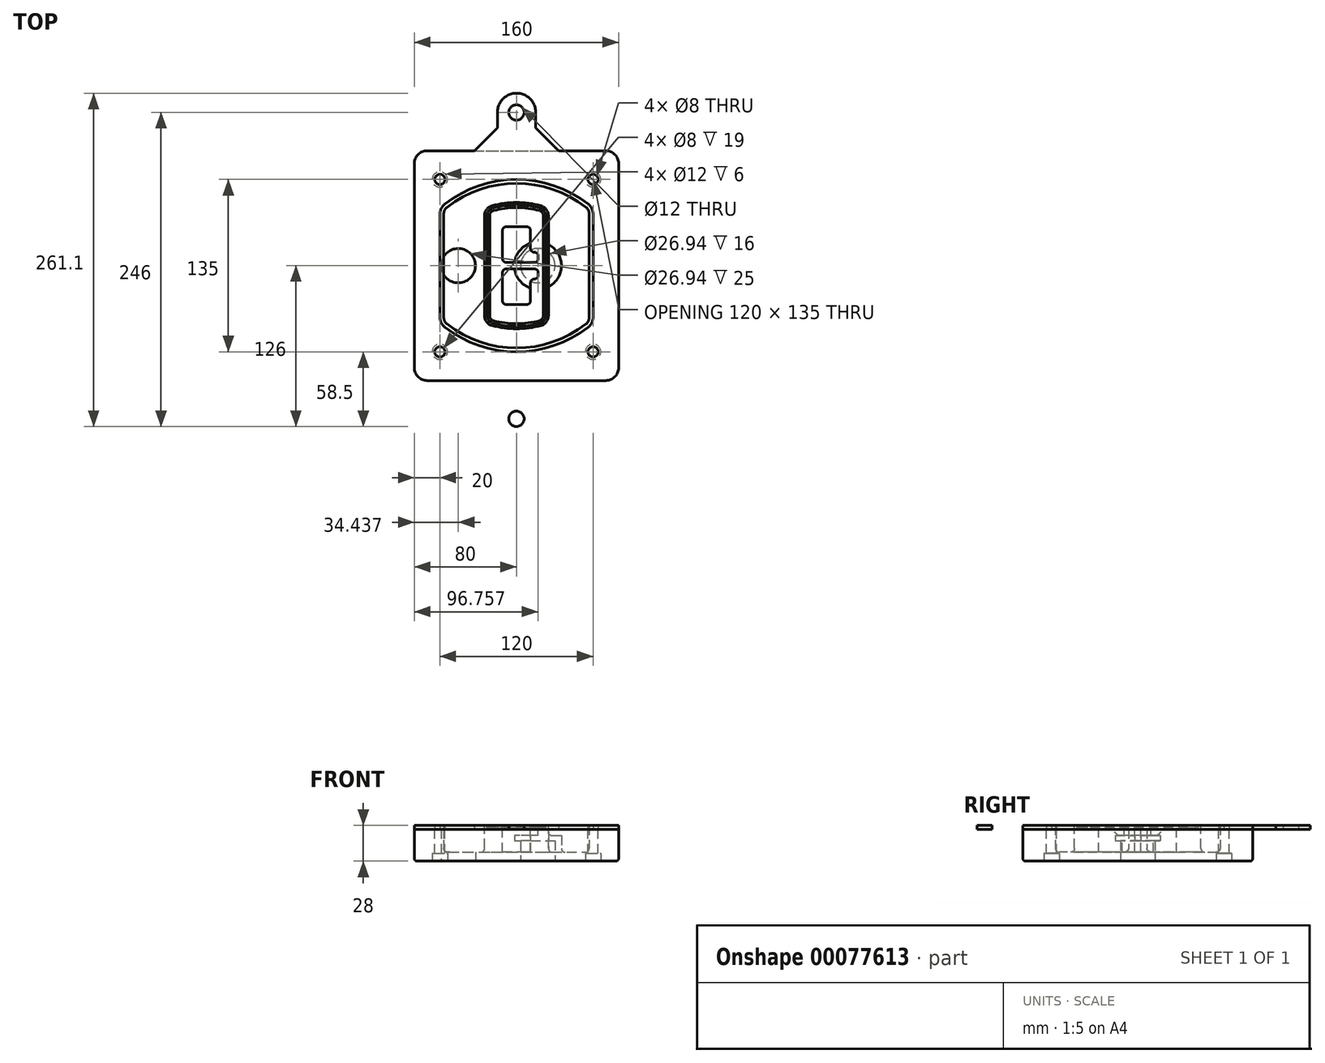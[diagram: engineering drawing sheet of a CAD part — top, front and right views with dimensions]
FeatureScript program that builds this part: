
annotation { "Feature Type Name" : "Feature", "Feature Type Description" : "" }
export const myFeature = defineFeature(function(context is Context, id is Id, definition is map)
    precondition{}
    {
        {
            var Q0;
            Q0=qCreatedBy(makeId("Top.planeOp"),FACE);
            var sketch = newSketch(context, id + "F0", { "sketchPlane" : qUnion([Q0])});
            skPoint(sketch, "E0.rect.middle", {"position": v(0, 0) * mm});
            skLineSegment(sketch, "E1.bottom", {"start": v(-70, -90) * mm, "end": v(70, -90) * mm});
            skLineSegment(sketch, "E1.top", {"start": v(-70, 90) * mm, "end": v(70, 90) * mm});
            skLineSegment(sketch, "E1.left", {"start": v(-80, -80) * mm, "end": v(-80, 80) * mm});
            skLineSegment(sketch, "E1.right", {"start": v(80, -80) * mm, "end": v(80, 80) * mm});
            skLineSegment(sketch, "E2", {"start": v(-80, 90) * mm, "end": v(80, -90) * mm, "construction": true});
            skLineSegment(sketch, "E3", {"start": v(80, 90) * mm, "end": v(-80, -90) * mm, "construction": true});
            skCircle(sketch, "E4", {"center": v(-60, 67.5) * mm, "radius": 4 * mm});
            skCircle(sketch, "E5", {"center": v(60, 67.5) * mm, "radius": 4 * mm});
            skCircle(sketch, "E6", {"center": v(60, -67.5) * mm, "radius": 4 * mm});
            skCircle(sketch, "E7", {"center": v(-60, -67.5) * mm, "radius": 4 * mm});
            skLineSegment(sketch, "E8", {"start": v(-60, 67.5) * mm, "end": v(60, 67.5) * mm, "construction": true});
            skLineSegment(sketch, "E9", {"start": v(60, 67.5) * mm, "end": v(60, -67.5) * mm, "construction": true});
            skLineSegment(sketch, "E10", {"start": v(60, -67.5) * mm, "end": v(-60, -67.5) * mm, "construction": true});
            skLineSegment(sketch, "E11", {"start": v(-60, -67.5) * mm, "end": v(-60, 67.5) * mm, "construction": true});
            skLineSegment(sketch, "E12", {"start": v(-60, 40.3) * mm, "end": v(-60, -40.3) * mm});
            skLineSegment(sketch, "E13", {"start": v(60, 40.3) * mm, "end": v(60, -40.3) * mm});
            skArc(sketch, "E14", {"start": v(56.15, 48.18) * mm, "mid": v(0, 67.5) * mm, "end": v(-56.15, 48.18) * mm});
            skArc(sketch, "E15", {"start": v(-56.15, -48.18) * mm, "mid": v(0, -67.5) * mm, "end": v(56.15, -48.18) * mm});
            skLineSegment(sketch, "E16", {"start": v(-60, 0) * mm, "end": v(60, 0) * mm, "construction": true});
            skPoint(sketch, "E17.visualSharp", {"position": v(-60, -45) * mm});
            skArc(sketch, "E17.filletArc", {"start": v(-60, -40.3) * mm, "mid": v(-58.99, -44.68) * mm, "end": v(-56.15, -48.18) * mm});
            skPoint(sketch, "E18.visualSharp", {"position": v(-60, 45) * mm});
            skArc(sketch, "E18.filletArc", {"start": v(-56.15, 48.18) * mm, "mid": v(-58.99, 44.68) * mm, "end": v(-60, 40.3) * mm});
            skPoint(sketch, "E19.visualSharp", {"position": v(60, 45) * mm});
            skArc(sketch, "E19.filletArc", {"start": v(60, 40.3) * mm, "mid": v(58.99, 44.68) * mm, "end": v(56.15, 48.18) * mm});
            skPoint(sketch, "E20.visualSharp", {"position": v(60, -45) * mm});
            skArc(sketch, "E20.filletArc", {"start": v(56.15, -48.18) * mm, "mid": v(58.99, -44.68) * mm, "end": v(60, -40.3) * mm});
            skPoint(sketch, "E21.visualSharp", {"position": v(-80, 90) * mm});
            skArc(sketch, "E21.filletArc", {"start": v(-70, 90) * mm, "mid": v(-77.07, 87.07) * mm, "end": v(-80, 80) * mm});
            skPoint(sketch, "E22.visualSharp", {"position": v(80, 90) * mm});
            skArc(sketch, "E22.filletArc", {"start": v(80, 80) * mm, "mid": v(77.07, 87.07) * mm, "end": v(70, 90) * mm});
            skPoint(sketch, "E23.visualSharp", {"position": v(80, -90) * mm});
            skArc(sketch, "E23.filletArc", {"start": v(70, -90) * mm, "mid": v(77.07, -87.07) * mm, "end": v(80, -80) * mm});
            skPoint(sketch, "E24.visualSharp", {"position": v(-80, -90) * mm});
            skArc(sketch, "E24.filletArc", {"start": v(-80, -80) * mm, "mid": v(-77.07, -87.07) * mm, "end": v(-70, -90) * mm});
            skArc(sketch, "E25.0", {"start": v(57, 40.3) * mm, "mid": v(56.3, 43.36) * mm, "end": v(54.3, 45.81) * mm});
            skLineSegment(sketch, "E25.1", {"start": v(57, 40.3) * mm, "end": v(57, -40.3) * mm});
            skArc(sketch, "E25.2", {"start": v(54.3, -45.81) * mm, "mid": v(56.3, -43.36) * mm, "end": v(57, -40.3) * mm});
            skArc(sketch, "E25.3", {"start": v(-54.3, -45.81) * mm, "mid": v(0, -64.5) * mm, "end": v(54.3, -45.81) * mm});
            skArc(sketch, "E25.4", {"start": v(-57, -40.3) * mm, "mid": v(-56.3, -43.36) * mm, "end": v(-54.3, -45.81) * mm});
            skArc(sketch, "E25.5", {"start": v(54.3, 45.81) * mm, "mid": v(0, 64.5) * mm, "end": v(-54.3, 45.81) * mm});
            skLineSegment(sketch, "E25.6", {"start": v(-57, 40.3) * mm, "end": v(-57, -40.3) * mm});
            skArc(sketch, "E25.7", {"start": v(-54.3, 45.81) * mm, "mid": v(-56.3, 43.36) * mm, "end": v(-57, 40.3) * mm});
            skArc(sketch, "E26.0", {"start": v(-58.62, 51.33) * mm, "mid": v(-62.58, 46.43) * mm, "end": v(-64, 40.3) * mm});
            skArc(sketch, "E26.1", {"start": v(58.62, 51.33) * mm, "mid": v(0, 71.5) * mm, "end": v(-58.62, 51.33) * mm});
            skArc(sketch, "E26.2", {"start": v(64, 40.3) * mm, "mid": v(62.58, 46.43) * mm, "end": v(58.62, 51.33) * mm});
            skLineSegment(sketch, "E26.3", {"start": v(64, 40.3) * mm, "end": v(64, -40.3) * mm});
            skArc(sketch, "E26.4", {"start": v(58.62, -51.33) * mm, "mid": v(62.58, -46.43) * mm, "end": v(64, -40.3) * mm});
            skLineSegment(sketch, "E26.5", {"start": v(-64, 40.3) * mm, "end": v(-64, -40.3) * mm});
            skArc(sketch, "E26.6", {"start": v(-58.62, -51.33) * mm, "mid": v(0, -71.5) * mm, "end": v(58.62, -51.33) * mm});
            skArc(sketch, "E26.7", {"start": v(-64, -40.3) * mm, "mid": v(-62.58, -46.43) * mm, "end": v(-58.62, -51.33) * mm});
            skSolve(sketch);
        }
        {
            var Q0;
            Q0=makeQuery(id+"F0.imprint","IMPRINT",FACE,{"disambiguationData":[TD([[makeQuery(id+"F0.imprint","IMPRINT",EDGE,{"derivedFrom":sQuery(id+"F0.wireOp",EDGE,"E1.bottom")}),1.0]])]});
            var Q1;
            Q1=makeQuery(id+"F0.imprint","IMPRINT",FACE,{"disambiguationData":[TD([[makeQuery(id+"F0.imprint","IMPRINT",EDGE,{"derivedFrom":sQuery(id+"F0.wireOp",EDGE,"E12")}),1.0]])]});
            var Q2;
            Q2=makeQuery(id+"F0.imprint","IMPRINT",FACE,{"disambiguationData":[TD([[makeQuery(id+"F0.imprint","IMPRINT",EDGE,{"derivedFrom":sQuery(id+"F0.wireOp",EDGE,"E25.0")}),1.0]])]});
            var Q3;
            Q3=makeQuery(id+"F0.imprint","IMPRINT",FACE,{"disambiguationData":[TD([[makeQuery(id+"F0.imprint","IMPRINT",EDGE,{"derivedFrom":sQuery(id+"F0.wireOp",EDGE,"E12")}),-1.0]])]});
            extrude(context, id + "F1", {"entities" : qUnion([Q0, Q1, Q2, Q3]), "oppositeDirection" : true, "depth" : 25 * mm});
        }
        {
            var Q0;
            Q0=makeQuery(id+"F0.imprint","IMPRINT",FACE,{"disambiguationData":[TD([[makeQuery(id+"F0.imprint","IMPRINT",EDGE,{"derivedFrom":sQuery(id+"F0.wireOp",EDGE,"E12")}),1.0]])]});
            extrude(context, id + "F2", {"entities" : qUnion([Q0]), "operationType" : NewBodyOperationType.ADD, "depth" : 3 * mm});
        }
        {
            var Q0;
            Q0=makeQuery(id+"F0.imprint","IMPRINT",FACE,{"disambiguationData":[TD([[makeQuery(id+"F0.imprint","IMPRINT",EDGE,{"derivedFrom":sQuery(id+"F0.wireOp",EDGE,"E25.0")}),1.0]])]});
            extrude(context, id + "F3", {"entities" : qUnion([Q0]), "operationType" : NewBodyOperationType.REMOVE, "oppositeDirection" : true, "depth" : 18 * mm});
        }
        {
            var Q0;
            Q0=makeQuery(id+"F2.opExtrude","CAP_FACE",FACE,{"disambiguationData":[OSD([sQuery(id+"F0.wireOp",EDGE,"E12"),sQuery(id+"F0.wireOp",EDGE,"E13"),sQuery(id+"F0.wireOp",EDGE,"E14"),sQuery(id+"F0.wireOp",EDGE,"E15"),sQuery(id+"F0.wireOp",EDGE,"E17.filletArc"),sQuery(id+"F0.wireOp",EDGE,"E18.filletArc"),sQuery(id+"F0.wireOp",EDGE,"E19.filletArc"),sQuery(id+"F0.wireOp",EDGE,"E20.filletArc"),sQuery(id+"F0.wireOp",EDGE,"E25.0"),sQuery(id+"F0.wireOp",EDGE,"E25.1"),sQuery(id+"F0.wireOp",EDGE,"E25.2"),sQuery(id+"F0.wireOp",EDGE,"E25.3"),sQuery(id+"F0.wireOp",EDGE,"E25.4"),sQuery(id+"F0.wireOp",EDGE,"E25.5"),sQuery(id+"F0.wireOp",EDGE,"E25.6"),sQuery(id+"F0.wireOp",EDGE,"E25.7")])],"isStart":false});
            var sketch = newSketch(context, id + "F4", { "sketchPlane" : qUnion([Q0])});
            skArc(sketch, "E27.0", {"start": v(-19.08, -46.97) * mm, "mid": v(0, -49.5) * mm, "end": v(19.08, -46.97) * mm});
            skArc(sketch, "E28.0", {"start": v(19.08, 46.97) * mm, "mid": v(0, 49.5) * mm, "end": v(-19.08, 46.97) * mm});
            skLineSegment(sketch, "E29", {"start": v(-25, 39.25) * mm, "end": v(-25, -39.25) * mm});
            skLineSegment(sketch, "E30", {"start": v(25, 39.25) * mm, "end": v(25, -39.25) * mm});
            skLineSegment(sketch, "E31", {"start": v(-25, 45.1) * mm, "end": v(25, 45.1) * mm, "construction": true});
            skLineSegment(sketch, "E32", {"start": v(-25, -45.1) * mm, "end": v(25, -45.1) * mm, "construction": true});
            skPoint(sketch, "E33.visualSharp", {"position": v(-25, 45.1) * mm});
            skArc(sketch, "E33.filletArc", {"start": v(-19.08, 46.97) * mm, "mid": v(-23.35, 44.11) * mm, "end": v(-25, 39.25) * mm});
            skPoint(sketch, "E34.visualSharp", {"position": v(25, 45.1) * mm});
            skArc(sketch, "E34.filletArc", {"start": v(25, 39.25) * mm, "mid": v(23.35, 44.11) * mm, "end": v(19.08, 46.97) * mm});
            skPoint(sketch, "E35.visualSharp", {"position": v(25, -45.1) * mm});
            skArc(sketch, "E35.filletArc", {"start": v(19.08, -46.97) * mm, "mid": v(23.35, -44.11) * mm, "end": v(25, -39.25) * mm});
            skPoint(sketch, "E36.visualSharp", {"position": v(-25, -45.1) * mm});
            skArc(sketch, "E36.filletArc", {"start": v(-25, -39.25) * mm, "mid": v(-23.35, -44.11) * mm, "end": v(-19.08, -46.97) * mm});
            skArc(sketch, "E37.0", {"start": v(54.3, 45.81) * mm, "mid": v(0, 64.5) * mm, "end": v(-54.3, 45.81) * mm});
            skArc(sketch, "E37.1", {"start": v(-54.3, 45.81) * mm, "mid": v(-56.3, 43.36) * mm, "end": v(-57, 40.3) * mm});
            skLineSegment(sketch, "E37.2", {"start": v(-57, 40.3) * mm, "end": v(-57, -40.3) * mm});
            skArc(sketch, "E37.3", {"start": v(-57, -40.3) * mm, "mid": v(-56.3, -43.36) * mm, "end": v(-54.3, -45.81) * mm});
            skArc(sketch, "E37.4", {"start": v(-54.3, -45.81) * mm, "mid": v(0, -64.5) * mm, "end": v(54.3, -45.81) * mm});
            skArc(sketch, "E37.5", {"start": v(54.3, -45.81) * mm, "mid": v(56.3, -43.36) * mm, "end": v(57, -40.3) * mm});
            skLineSegment(sketch, "E37.6", {"start": v(57, 40.3) * mm, "end": v(57, -40.3) * mm});
            skArc(sketch, "E37.7", {"start": v(57, 40.3) * mm, "mid": v(56.3, 43.36) * mm, "end": v(54.3, 45.81) * mm});
            skLineSegment(sketch, "E38.0", {"start": v(23, 39.25) * mm, "end": v(23, -39.25) * mm});
            skArc(sketch, "E38.1", {"start": v(18.56, -45.04) * mm, "mid": v(21.76, -42.9) * mm, "end": v(23, -39.25) * mm});
            skArc(sketch, "E38.2", {"start": v(-18.56, -45.04) * mm, "mid": v(0, -47.5) * mm, "end": v(18.56, -45.04) * mm});
            skArc(sketch, "E38.3", {"start": v(-23, -39.25) * mm, "mid": v(-21.76, -42.9) * mm, "end": v(-18.56, -45.04) * mm});
            skLineSegment(sketch, "E38.4", {"start": v(-23, 39.25) * mm, "end": v(-23, -39.25) * mm});
            skArc(sketch, "E38.5", {"start": v(23, 39.25) * mm, "mid": v(21.76, 42.9) * mm, "end": v(18.56, 45.04) * mm});
            skArc(sketch, "E38.6", {"start": v(-18.56, 45.04) * mm, "mid": v(-21.76, 42.9) * mm, "end": v(-23, 39.25) * mm});
            skArc(sketch, "E38.7", {"start": v(18.56, 45.04) * mm, "mid": v(0, 47.5) * mm, "end": v(-18.56, 45.04) * mm});
            skArc(sketch, "E39.0", {"start": v(21, 39.25) * mm, "mid": v(20.18, 41.68) * mm, "end": v(18.04, 43.1) * mm});
            skLineSegment(sketch, "E39.1", {"start": v(21, 39.25) * mm, "end": v(21, -39.25) * mm});
            skArc(sketch, "E39.2", {"start": v(18.04, -43.1) * mm, "mid": v(20.18, -41.68) * mm, "end": v(21, -39.25) * mm});
            skArc(sketch, "E39.3", {"start": v(-18.04, -43.1) * mm, "mid": v(0, -45.5) * mm, "end": v(18.04, -43.1) * mm});
            skArc(sketch, "E39.4", {"start": v(-21, -39.25) * mm, "mid": v(-20.18, -41.68) * mm, "end": v(-18.04, -43.1) * mm});
            skArc(sketch, "E39.5", {"start": v(18.04, 43.1) * mm, "mid": v(0, 45.5) * mm, "end": v(-18.04, 43.1) * mm});
            skLineSegment(sketch, "E39.6", {"start": v(-21, 39.25) * mm, "end": v(-21, -39.25) * mm});
            skArc(sketch, "E39.7", {"start": v(-18.04, 43.1) * mm, "mid": v(-20.18, 41.68) * mm, "end": v(-21, 39.25) * mm});
            skLineSegment(sketch, "E40", {"start": v(-25, 0) * mm, "end": v(25, 0) * mm, "construction": true});
            skLineSegment(sketch, "E41", {"start": v(-11, 5.5) * mm, "end": v(-11, 27.5) * mm});
            skLineSegment(sketch, "E42", {"start": v(-8, 30.5) * mm, "end": v(8, 30.5) * mm});
            skLineSegment(sketch, "E43", {"start": v(11, 27.5) * mm, "end": v(11, 13.5) * mm});
            skLineSegment(sketch, "E44", {"start": v(14, 10.5) * mm, "end": v(14, 10.5) * mm});
            skLineSegment(sketch, "E45", {"start": v(17, 7.5) * mm, "end": v(17, 5.5) * mm});
            skLineSegment(sketch, "E46", {"start": v(14, 2.5) * mm, "end": v(-8, 2.5) * mm});
            skPoint(sketch, "E47.visualSharp", {"position": v(-11, 30.5) * mm});
            skArc(sketch, "E47.filletArc", {"start": v(-8, 30.5) * mm, "mid": v(-10.12, 29.62) * mm, "end": v(-11, 27.5) * mm});
            skPoint(sketch, "E48.visualSharp", {"position": v(11, 30.5) * mm});
            skArc(sketch, "E48.filletArc", {"start": v(11, 27.5) * mm, "mid": v(10.12, 29.62) * mm, "end": v(8, 30.5) * mm});
            skPoint(sketch, "E49.visualSharp", {"position": v(11, 10.5) * mm});
            skArc(sketch, "E49.filletArc", {"start": v(11, 13.5) * mm, "mid": v(11.88, 11.38) * mm, "end": v(14, 10.5) * mm});
            skPoint(sketch, "E50.visualSharp", {"position": v(17, 10.5) * mm});
            skArc(sketch, "E50.filletArc", {"start": v(17, 7.5) * mm, "mid": v(16.12, 9.62) * mm, "end": v(14, 10.5) * mm});
            skPoint(sketch, "E51.visualSharp", {"position": v(17, 2.5) * mm});
            skArc(sketch, "E51.filletArc", {"start": v(14, 2.5) * mm, "mid": v(16.12, 3.38) * mm, "end": v(17, 5.5) * mm});
            skPoint(sketch, "E52.visualSharp", {"position": v(-11, 2.5) * mm});
            skArc(sketch, "E52.filletArc", {"start": v(-11, 5.5) * mm, "mid": v(-10.12, 3.38) * mm, "end": v(-8, 2.5) * mm});
            skLineSegment(sketch, "E53.0.MirrorCS", {"start": v(14, -2.5) * mm, "end": v(-8, -2.5) * mm});
            skArc(sketch, "E54.0.MirrorCS", {"start": v(-11, -5.5) * mm, "mid": v(-10.12, -3.38) * mm, "end": v(-8, -2.5) * mm});
            skLineSegment(sketch, "E55.0.MirrorCS", {"start": v(-11, -5.5) * mm, "end": v(-11, -27.5) * mm});
            skArc(sketch, "E56.0.MirrorCS", {"start": v(-8, -30.5) * mm, "mid": v(-10.12, -29.62) * mm, "end": v(-11, -27.5) * mm});
            skLineSegment(sketch, "E57.0.MirrorCS", {"start": v(-8, -30.5) * mm, "end": v(8, -30.5) * mm});
            skArc(sketch, "E58.0.MirrorCS", {"start": v(11, -27.5) * mm, "mid": v(10.12, -29.62) * mm, "end": v(8, -30.5) * mm});
            skLineSegment(sketch, "E59.0.MirrorCS", {"start": v(11, -27.5) * mm, "end": v(11, -13.5) * mm});
            skArc(sketch, "E60.0.MirrorCS", {"start": v(11, -13.5) * mm, "mid": v(11.88, -11.38) * mm, "end": v(14, -10.5) * mm});
            skArc(sketch, "E61.0.MirrorCS", {"start": v(17, -7.5) * mm, "mid": v(16.12, -9.62) * mm, "end": v(14, -10.5) * mm});
            skLineSegment(sketch, "E62.0.MirrorCS", {"start": v(17, -7.5) * mm, "end": v(17, -5.5) * mm});
            skArc(sketch, "E63.0.MirrorCS", {"start": v(14, -2.5) * mm, "mid": v(16.12, -3.38) * mm, "end": v(17, -5.5) * mm});
            skSolve(sketch);
        }
        {
            var Q0;
            Q0=makeQuery(id+"F4.imprint","IMPRINT",FACE,{"disambiguationData":[TD([[makeQuery(id+"F4.imprint","IMPRINT",EDGE,{"derivedFrom":sQuery(id+"F4.wireOp",EDGE,"E27.0")}),1.0]])]});
            var Q1;
            Q1=makeQuery(id+"F4.imprint","IMPRINT",FACE,{"disambiguationData":[TD([[makeQuery(id+"F4.imprint","IMPRINT",EDGE,{"derivedFrom":sQuery(id+"F4.wireOp",EDGE,"E38.0")}),-1.0]])]});
            var Q2;
            Q2=makeQuery(id+"F4.imprint","IMPRINT",FACE,{"disambiguationData":[TD([[makeQuery(id+"F4.imprint","IMPRINT",EDGE,{"derivedFrom":sQuery(id+"F4.wireOp",EDGE,"E39.0")}),1.0]])]});
            extrude(context, id + "F5", {"entities" : qUnion([Q0, Q1, Q2]), "operationType" : NewBodyOperationType.ADD, "endBound" : BoundingType.UP_TO_NEXT, "oppositeDirection" : true, "depth" : 25 * mm});
        }
        {
            var Q0;
            Q0=makeQuery(id+"F4.imprint","IMPRINT",FACE,{"disambiguationData":[TD([[makeQuery(id+"F4.imprint","IMPRINT",EDGE,{"derivedFrom":sQuery(id+"F4.wireOp",EDGE,"E38.0")}),-1.0]])]});
            extrude(context, id + "F6", {"entities" : qUnion([Q0]), "operationType" : NewBodyOperationType.REMOVE, "oppositeDirection" : true, "depth" : 2 * mm});
        }
        {
            var Q0;
            Q0=makeQuery(id+"F1.opExtrude","CAP_FACE",FACE,{"disambiguationData":[OSD([sQuery(id+"F0.wireOp",EDGE,"E1.bottom"),sQuery(id+"F0.wireOp",EDGE,"E1.top"),sQuery(id+"F0.wireOp",EDGE,"E1.left"),sQuery(id+"F0.wireOp",EDGE,"E1.right"),sQuery(id+"F0.wireOp",EDGE,"E4"),sQuery(id+"F0.wireOp",EDGE,"E5"),sQuery(id+"F0.wireOp",EDGE,"E6"),sQuery(id+"F0.wireOp",EDGE,"E7"),sQuery(id+"F0.wireOp",EDGE,"E21.filletArc"),sQuery(id+"F0.wireOp",EDGE,"E22.filletArc"),sQuery(id+"F0.wireOp",EDGE,"E23.filletArc"),sQuery(id+"F0.wireOp",EDGE,"E24.filletArc")])],"isStart":false});
            var sketch = newSketch(context, id + "F7", { "sketchPlane" : qUnion([Q0])});
            skCircle(sketch, "E64", {"center": v(16.76, 0) * mm, "radius": 13.47 * mm});
            skCircle(sketch, "E65", {"center": v(-45.56, 0) * mm, "radius": 13.47 * mm});
            skLineSegment(sketch, "E66", {"start": v(80, 0) * mm, "end": v(-80, 0) * mm});
            skCircle(sketch, "E67", {"center": v(16.76, 0) * mm, "radius": 18.47 * mm});
            skCircle(sketch, "E68", {"center": v(60, -67.5) * mm, "radius": 6 * mm});
            skCircle(sketch, "E69", {"center": v(-60, -67.5) * mm, "radius": 6 * mm});
            skCircle(sketch, "E70", {"center": v(-60, 67.5) * mm, "radius": 6 * mm});
            skCircle(sketch, "E71", {"center": v(60, 67.5) * mm, "radius": 6 * mm});
            skSolve(sketch);
        }
        {
            var Q0;
            {var subQ1=sQuery(id+"F7.wireOp",EDGE,"E66");var subQ4=sQuery(id+"F7.wireOp",EDGE,"E64");var subQ6=makeQuery(id+"F7.imprint","INTERSECT",VERTEX,{"disambiguationData":[OD(0.0)],"derivedFrom":[subQ4,subQ1]});Q0=makeQuery(id+"F7.imprint","IMPRINT",FACE,{"disambiguationData":[TD([[makeQuery(id+"F7.imprint","IMPRINT",EDGE,{"disambiguationData":[TD([[subQ6,-1.0]])],"derivedFrom":subQ4}),-1.0]])]});}
            var Q1;
            {var subQ0=sQuery(id+"F7.wireOp",EDGE,"E66");var subQ1=sQuery(id+"F7.wireOp",EDGE,"E64");var subQ3=makeQuery(id+"F7.imprint","INTERSECT",VERTEX,{"disambiguationData":[OD(0.0)],"derivedFrom":[subQ1,subQ0]});Q1=makeQuery(id+"F7.imprint","IMPRINT",FACE,{"disambiguationData":[TD([[makeQuery(id+"F7.imprint","IMPRINT",EDGE,{"disambiguationData":[TD([[subQ3,-1.0]])],"derivedFrom":subQ1}),1.0]])]});}
            var Q2;
            {var subQ0=sQuery(id+"F7.wireOp",EDGE,"E66");var subQ1=sQuery(id+"F7.wireOp",EDGE,"E64");var subQ3=makeQuery(id+"F7.imprint","INTERSECT",VERTEX,{"disambiguationData":[OD(0.0)],"derivedFrom":[subQ1,subQ0]});Q2=makeQuery(id+"F7.imprint","IMPRINT",FACE,{"disambiguationData":[TD([[makeQuery(id+"F7.imprint","IMPRINT",EDGE,{"disambiguationData":[TD([[subQ3,1.0]])],"derivedFrom":subQ1}),1.0]])]});}
            var Q3;
            {var subQ1=sQuery(id+"F7.wireOp",EDGE,"E66");var subQ4=sQuery(id+"F7.wireOp",EDGE,"E64");var subQ6=makeQuery(id+"F7.imprint","INTERSECT",VERTEX,{"disambiguationData":[OD(0.0)],"derivedFrom":[subQ4,subQ1]});Q3=makeQuery(id+"F7.imprint","IMPRINT",FACE,{"disambiguationData":[TD([[makeQuery(id+"F7.imprint","IMPRINT",EDGE,{"disambiguationData":[TD([[subQ6,1.0]])],"derivedFrom":subQ4}),-1.0]])]});}
            extrude(context, id + "F8", {"entities" : qUnion([Q0, Q1, Q2, Q3]), "operationType" : NewBodyOperationType.ADD, "oppositeDirection" : true, "depth" : 20 * mm});
        }
        {
            var Q0;
            {var subQ0=sQuery(id+"F7.wireOp",EDGE,"E66");var subQ1=sQuery(id+"F7.wireOp",EDGE,"E64");var subQ3=makeQuery(id+"F7.imprint","INTERSECT",VERTEX,{"disambiguationData":[OD(0.0)],"derivedFrom":[subQ1,subQ0]});Q0=makeQuery(id+"F7.imprint","IMPRINT",FACE,{"disambiguationData":[TD([[makeQuery(id+"F7.imprint","IMPRINT",EDGE,{"disambiguationData":[TD([[subQ3,-1.0]])],"derivedFrom":subQ1}),1.0]])]});}
            var Q1;
            {var subQ0=sQuery(id+"F7.wireOp",EDGE,"E66");var subQ1=sQuery(id+"F7.wireOp",EDGE,"E64");var subQ3=makeQuery(id+"F7.imprint","INTERSECT",VERTEX,{"disambiguationData":[OD(0.0)],"derivedFrom":[subQ1,subQ0]});Q1=makeQuery(id+"F7.imprint","IMPRINT",FACE,{"disambiguationData":[TD([[makeQuery(id+"F7.imprint","IMPRINT",EDGE,{"disambiguationData":[TD([[subQ3,1.0]])],"derivedFrom":subQ1}),1.0]])]});}
            extrude(context, id + "F9", {"entities" : qUnion([Q0, Q1]), "operationType" : NewBodyOperationType.REMOVE, "oppositeDirection" : true, "depth" : 16 * mm});
        }
        {
            var Q0;
            {var subQ0=sQuery(id+"F7.wireOp",EDGE,"E66");var subQ1=sQuery(id+"F7.wireOp",EDGE,"E65");var subQ3=makeQuery(id+"F7.imprint","INTERSECT",VERTEX,{"disambiguationData":[OD(0.0)],"derivedFrom":[subQ1,subQ0]});Q0=makeQuery(id+"F7.imprint","IMPRINT",FACE,{"disambiguationData":[TD([[makeQuery(id+"F7.imprint","IMPRINT",EDGE,{"disambiguationData":[TD([[subQ3,-1.0]])],"derivedFrom":subQ1}),1.0]])]});}
            var Q1;
            {var subQ0=sQuery(id+"F7.wireOp",EDGE,"E66");var subQ1=sQuery(id+"F7.wireOp",EDGE,"E65");var subQ3=makeQuery(id+"F7.imprint","INTERSECT",VERTEX,{"disambiguationData":[OD(0.0)],"derivedFrom":[subQ1,subQ0]});Q1=makeQuery(id+"F7.imprint","IMPRINT",FACE,{"disambiguationData":[TD([[makeQuery(id+"F7.imprint","IMPRINT",EDGE,{"disambiguationData":[TD([[subQ3,1.0]])],"derivedFrom":subQ1}),1.0]])]});}
            extrude(context, id + "F10", {"entities" : qUnion([Q0, Q1]), "operationType" : NewBodyOperationType.REMOVE, "oppositeDirection" : true, "depth" : 25 * mm});
        }
        {
            var Q0;
            Q0=makeQuery(id+"F7.imprint","IMPRINT",FACE,{"disambiguationData":[TD([[makeQuery(id+"F7.imprint","IMPRINT",EDGE,{"derivedFrom":sQuery(id+"F7.wireOp",EDGE,"E68")}),1.0]])]});
            var Q1;
            Q1=makeQuery(id+"F7.imprint","IMPRINT",FACE,{"disambiguationData":[TD([[makeQuery(id+"F7.imprint","IMPRINT",EDGE,{"derivedFrom":makeQuery(id+"F1.opExtrude","CAP_EDGE",EDGE,{"disambiguationData":[OSD([sQuery(id+"F0.wireOp",EDGE,"E5")])],"isStart":false})}),-1.0]])]});
            var Q2;
            Q2=makeQuery(id+"F7.imprint","IMPRINT",FACE,{"disambiguationData":[TD([[makeQuery(id+"F7.imprint","IMPRINT",EDGE,{"derivedFrom":sQuery(id+"F7.wireOp",EDGE,"E69")}),1.0]])]});
            var Q3;
            Q3=makeQuery(id+"F7.imprint","IMPRINT",FACE,{"disambiguationData":[TD([[makeQuery(id+"F7.imprint","IMPRINT",EDGE,{"derivedFrom":makeQuery(id+"F1.opExtrude","CAP_EDGE",EDGE,{"disambiguationData":[OSD([sQuery(id+"F0.wireOp",EDGE,"E4")])],"isStart":false})}),-1.0]])]});
            var Q4;
            Q4=makeQuery(id+"F7.imprint","IMPRINT",FACE,{"disambiguationData":[TD([[makeQuery(id+"F7.imprint","IMPRINT",EDGE,{"derivedFrom":sQuery(id+"F7.wireOp",EDGE,"E70")}),1.0]])]});
            var Q5;
            Q5=makeQuery(id+"F7.imprint","IMPRINT",FACE,{"disambiguationData":[TD([[makeQuery(id+"F7.imprint","IMPRINT",EDGE,{"derivedFrom":makeQuery(id+"F1.opExtrude","CAP_EDGE",EDGE,{"disambiguationData":[OSD([sQuery(id+"F0.wireOp",EDGE,"E7")])],"isStart":false})}),-1.0]])]});
            var Q6;
            Q6=makeQuery(id+"F7.imprint","IMPRINT",FACE,{"disambiguationData":[TD([[makeQuery(id+"F7.imprint","IMPRINT",EDGE,{"derivedFrom":sQuery(id+"F7.wireOp",EDGE,"E71")}),1.0]])]});
            var Q7;
            Q7=makeQuery(id+"F7.imprint","IMPRINT",FACE,{"disambiguationData":[TD([[makeQuery(id+"F7.imprint","IMPRINT",EDGE,{"derivedFrom":makeQuery(id+"F1.opExtrude","CAP_EDGE",EDGE,{"disambiguationData":[OSD([sQuery(id+"F0.wireOp",EDGE,"E6")])],"isStart":false})}),-1.0]])]});
            extrude(context, id + "F11", {"entities" : qUnion([Q0, Q1, Q2, Q3, Q4, Q5, Q6, Q7]), "operationType" : NewBodyOperationType.REMOVE, "oppositeDirection" : true, "depth" : 6 * mm});
        }
        {
            var Q0;
            Q0=makeQuery(id+"F9.boolean.opBoolean","COPY",FACE,{"derivedFrom":makeQuery(id+"F9.opExtrude","CAP_FACE",FACE,{"disambiguationData":[OSD([sQuery(id+"F7.wireOp",EDGE,"E64")])],"isStart":false})});
            var sketch = newSketch(context, id + "F12", { "sketchPlane" : qUnion([Q0])});
            skArc(sketch, "E72.0", {"start": v(11, 17.55) * mm, "mid": v(2.57, 11.82) * mm, "end": v(-1.54, 2.5) * mm});
            skArc(sketch, "E72.1", {"start": v(-1.54, -2.5) * mm, "mid": v(2.57, -11.82) * mm, "end": v(11, -17.55) * mm});
            skLineSegment(sketch, "E73", {"start": v(-1.54, -2.5) * mm, "end": v(14, -2.5) * mm});
            skLineSegment(sketch, "E74.0", {"start": v(14, 2.5) * mm, "end": v(-1.54, 2.5) * mm});
            skArc(sketch, "E74.1", {"start": v(14, 2.5) * mm, "mid": v(16.12, 3.38) * mm, "end": v(17, 5.5) * mm});
            skLineSegment(sketch, "E74.2", {"start": v(17, 7.5) * mm, "end": v(17, 5.5) * mm});
            skArc(sketch, "E74.3", {"start": v(17, 7.5) * mm, "mid": v(16.12, 9.62) * mm, "end": v(14, 10.5) * mm});
            skArc(sketch, "E74.4", {"start": v(11, 13.5) * mm, "mid": v(11.88, 11.38) * mm, "end": v(14, 10.5) * mm});
            skLineSegment(sketch, "E74.5", {"start": v(11, 17.55) * mm, "end": v(11, 13.5) * mm});
            skLineSegment(sketch, "E74.7", {"start": v(14, -2.5) * mm, "end": v(-1.54, -2.5) * mm});
            skArc(sketch, "E74.8", {"start": v(14, -2.5) * mm, "mid": v(16.12, -3.38) * mm, "end": v(17, -5.5) * mm});
            skLineSegment(sketch, "E74.9", {"start": v(17, -7.5) * mm, "end": v(17, -5.5) * mm});
            skArc(sketch, "E74.10", {"start": v(17, -7.5) * mm, "mid": v(16.12, -9.62) * mm, "end": v(14, -10.5) * mm});
            skArc(sketch, "E74.11", {"start": v(11, -13.5) * mm, "mid": v(11.88, -11.38) * mm, "end": v(14, -10.5) * mm});
            skLineSegment(sketch, "E74.12", {"start": v(11, -17.55) * mm, "end": v(11, -13.5) * mm});
            skPoint(sketch, "E75.orphan", {"position": v(11, -27.5) * mm});
            skPoint(sketch, "E76.orphan", {"position": v(-8, -2.5) * mm});
            skPoint(sketch, "E77.orphan", {"position": v(-8, 2.5) * mm});
            skPoint(sketch, "E78.orphan", {"position": v(11, 27.5) * mm});
            skSolve(sketch);
        }
        {
            var Q0;
            {var subQ7=sQuery(id+"F12.wireOp",EDGE,"E72.0");var subQ14=sQuery(id+"F12.wireOp",EDGE,"E72.1");var subQ16=sQuery(id+"F12.wireOp",EDGE,"E74.1");var subQ18=sQuery(id+"F12.wireOp",EDGE,"E74.8");Q0=qUnion([makeQuery(id+"F12.imprint","IMPRINT",FACE,{"disambiguationData":[TD([[makeQuery(id+"F12.imprint","IMPRINT",EDGE,{"derivedFrom":subQ7}),1.0]])]}),makeQuery(id+"F12.imprint","IMPRINT",FACE,{"disambiguationData":[TD([[makeQuery(id+"F12.imprint","IMPRINT",EDGE,{"derivedFrom":subQ14}),1.0]])]}),makeQuery(id+"F12.imprint","IMPRINT",FACE,{"disambiguationData":[TD([[makeQuery(id+"F12.imprint","IMPRINT",EDGE,{"derivedFrom":subQ16}),1.0]])]}),makeQuery(id+"F12.imprint","IMPRINT",FACE,{"disambiguationData":[TD([[makeQuery(id+"F12.imprint","IMPRINT",EDGE,{"derivedFrom":subQ18}),-1.0]])]})]);}
            var Q1;
            Q1=makeQuery(id+"F5.boolean.opBoolean","SPLIT",FACE,{"disambiguationData":[TD([makeQuery(id+"F5.opExtrude","SWEPT_FACE",FACE,{"disambiguationData":[OSD([sQuery(id+"F4.wireOp",EDGE,"E41")])]})])],"derivedFrom":makeQuery(id+"F3.boolean.opBoolean","COPY",FACE,{"derivedFrom":makeQuery(id+"F3.opExtrude","CAP_FACE",FACE,{"disambiguationData":[OSD([sQuery(id+"F0.wireOp",EDGE,"E25.0"),sQuery(id+"F0.wireOp",EDGE,"E25.1"),sQuery(id+"F0.wireOp",EDGE,"E25.2"),sQuery(id+"F0.wireOp",EDGE,"E25.3"),sQuery(id+"F0.wireOp",EDGE,"E25.4"),sQuery(id+"F0.wireOp",EDGE,"E25.5"),sQuery(id+"F0.wireOp",EDGE,"E25.6"),sQuery(id+"F0.wireOp",EDGE,"E25.7")])],"isStart":false})})});
            extrude(context, id + "F13", {"entities" : qUnion([Q0]), "operationType" : NewBodyOperationType.REMOVE, "endBound" : BoundingType.UP_TO_SURFACE, "endBoundEntityFace" : qUnion([Q1]), "depth" : 25 * mm});
        }
        {
            var Q0;
            Q0=makeQuery(id+"F3.boolean.opBoolean","COPY",EDGE,{"derivedFrom":makeQuery(id+"F3.opExtrude","CAP_EDGE",EDGE,{"disambiguationData":[OSD([sQuery(id+"F0.wireOp",EDGE,"E25.6")])],"isStart":false})});
            var Q1;
            Q1=makeQuery(id+"F8.boolean.opBoolean","INTERSECT",EDGE,{"derivedFrom":[makeQuery(id+"F5.opExtrude","SWEPT_FACE",FACE,{"disambiguationData":[OSD([sQuery(id+"F4.wireOp",EDGE,"E30")])]}),makeQuery(id+"F8.opExtrude","CAP_FACE",FACE,{"disambiguationData":[OSD([sQuery(id+"F7.wireOp",EDGE,"E67")])],"isStart":false})]});
            var Q2;
            Q2=makeQuery(id+"F8.boolean.opBoolean","INTERSECT",EDGE,{"disambiguationData":[OD(1.0)],"derivedFrom":[makeQuery(id+"F5.opExtrude","SWEPT_FACE",FACE,{"disambiguationData":[OSD([sQuery(id+"F4.wireOp",EDGE,"E30")])]}),makeQuery(id+"F8.opExtrude","SWEPT_FACE",FACE,{"disambiguationData":[OSD([sQuery(id+"F7.wireOp",EDGE,"E67")])]})]});
            var Q3;
            {var subQ0=sQuery(id+"F4.wireOp",EDGE,"E30");Q3=makeQuery(id+"F8.boolean.opBoolean","SPLIT",EDGE,{"disambiguationData":[TD([makeQuery(id+"F5.opExtrude","SWEPT_FACE",FACE,{"disambiguationData":[OSD([sQuery(id+"F4.wireOp",EDGE,"E35.filletArc")])]})])],"derivedFrom":makeQuery(id+"F5.opExtrude","CAP_EDGE",EDGE,{"disambiguationData":[OSD([subQ0])],"isStart":false})});}
            var Q4;
            {var subQ0=sQuery(id+"F0.wireOp",EDGE,"E25.7");var subQ1=sQuery(id+"F0.wireOp",EDGE,"E25.1");var subQ2=sQuery(id+"F0.wireOp",EDGE,"E25.6");var subQ3=sQuery(id+"F0.wireOp",EDGE,"E25.5");var subQ4=sQuery(id+"F0.wireOp",EDGE,"E25.4");var subQ5=sQuery(id+"F0.wireOp",EDGE,"E25.0");var subQ6=sQuery(id+"F0.wireOp",EDGE,"E25.2");var subQ7=sQuery(id+"F0.wireOp",EDGE,"E25.3");Q4=makeQuery(id+"F8.boolean.opBoolean","INTERSECT",EDGE,{"derivedFrom":[makeQuery(id+"F5.boolean.opBoolean","SPLIT",FACE,{"disambiguationData":[TD([makeQuery(id+"F2.opExtrude","SWEPT_FACE",FACE,{"disambiguationData":[OSD([subQ5])]})])],"derivedFrom":makeQuery(id+"F3.boolean.opBoolean","COPY",FACE,{"derivedFrom":makeQuery(id+"F3.opExtrude","CAP_FACE",FACE,{"disambiguationData":[OSD([subQ5,subQ1,subQ6,subQ7,subQ4,subQ3,subQ2,subQ0])],"isStart":false})})}),makeQuery(id+"F8.opExtrude","SWEPT_FACE",FACE,{"disambiguationData":[OSD([sQuery(id+"F7.wireOp",EDGE,"E67")])]})]});}
            var Q5;
            Q5=makeQuery(id+"F8.boolean.opBoolean","INTERSECT",EDGE,{"disambiguationData":[OD(0.0)],"derivedFrom":[makeQuery(id+"F5.opExtrude","SWEPT_FACE",FACE,{"disambiguationData":[OSD([sQuery(id+"F4.wireOp",EDGE,"E30")])]}),makeQuery(id+"F8.opExtrude","SWEPT_FACE",FACE,{"disambiguationData":[OSD([sQuery(id+"F7.wireOp",EDGE,"E67")])]})]});
            fillet(context, id + "F14", {"entities" : qUnion([Q0, Q1, Q2, Q3, Q4, Q5]), "radius" : 3 * mm, "tangentPropagation" : true, "allowEdgeOverflow" : false});
        }
        {
            var Q0;
            Q0=makeQuery(id+"F1.opExtrude","CAP_EDGE",EDGE,{"disambiguationData":[OSD([sQuery(id+"F0.wireOp",EDGE,"E1.bottom")])],"isStart":false});
            fillet(context, id + "F15", {"entities" : qUnion([Q0]), "radius" : 2 * mm, "tangentPropagation" : true, "allowEdgeOverflow" : false});
        }
        {
            var Q0;
            {var subQ0=sQuery(id+"F0.wireOp",EDGE,"E22.filletArc");var subQ1=sQuery(id+"F0.wireOp",EDGE,"E7");var subQ2=sQuery(id+"F0.wireOp",EDGE,"E6");var subQ3=sQuery(id+"F0.wireOp",EDGE,"E5");var subQ4=sQuery(id+"F0.wireOp",EDGE,"E4");var subQ5=sQuery(id+"F0.wireOp",EDGE,"E1.bottom");var subQ6=sQuery(id+"F0.wireOp",EDGE,"E21.filletArc");var subQ7=sQuery(id+"F0.wireOp",EDGE,"E1.top");var subQ8=sQuery(id+"F0.wireOp",EDGE,"E1.left");var subQ9=sQuery(id+"F0.wireOp",EDGE,"E1.right");var subQ10=sQuery(id+"F0.wireOp",EDGE,"E23.filletArc");var subQ11=sQuery(id+"F0.wireOp",EDGE,"E24.filletArc");Q0=makeQuery(id+"F2.boolean.opBoolean","SPLIT",FACE,{"disambiguationData":[TD([makeQuery(id+"F1.opExtrude","SWEPT_FACE",FACE,{"disambiguationData":[OSD([subQ5])]})])],"derivedFrom":makeQuery(id+"F1.opExtrude","CAP_FACE",FACE,{"disambiguationData":[OSD([subQ5,subQ7,subQ8,subQ9,subQ4,subQ3,subQ2,subQ1,subQ6,subQ0,subQ10,subQ11])],"isStart":true})});}
            var sketch = newSketch(context, id + "F16", { "sketchPlane" : qUnion([Q0])});
            skLineSegment(sketch, "E79", {"start": v(0, 90) * mm, "end": v(0, 120) * mm, "construction": true});
            skCircle(sketch, "E80", {"center": v(0, 120) * mm, "radius": 6 * mm});
            skArc(sketch, "E81", {"start": v(15.06, 120.03) * mm, "mid": v(0.06, 135.1) * mm, "end": v(-14.94, 120.03) * mm});
            skLineSegment(sketch, "E82", {"start": v(-14.94, 120.03) * mm, "end": v(-14.88, 108) * mm});
            skLineSegment(sketch, "E83", {"start": v(15.06, 120.03) * mm, "end": v(15.06, 108.03) * mm});
            skLineSegment(sketch, "E84", {"start": v(33.1, 90) * mm, "end": v(15.06, 108.03) * mm});
            skLineSegment(sketch, "E85", {"start": v(-32.82, 90) * mm, "end": v(-14.88, 108) * mm});
            skLineSegment(sketch, "E86", {"start": v(-80, 0) * mm, "end": v(80, 0) * mm, "construction": true});
            skLineSegment(sketch, "E87.MirrorCS", {"start": v(0, -90) * mm, "end": v(0, -120) * mm, "construction": true});
            skCircle(sketch, "E88.MirrorC", {"center": v(0, -120) * mm, "radius": 6 * mm});
            skArc(sketch, "E89.MirrorCS", {"start": v(15.06, -120.03) * mm, "mid": v(0.06, -135.1) * mm, "end": v(-14.94, -120.03) * mm});
            skLineSegment(sketch, "E90.MirrorCS", {"start": v(-32.82, -90) * mm, "end": v(-14.88, -108) * mm});
            skLineSegment(sketch, "E91.MirrorCS", {"start": v(15.06, -120.03) * mm, "end": v(15.06, -108.03) * mm});
            skLineSegment(sketch, "E92.MirrorCS", {"start": v(33.1, -90) * mm, "end": v(15.06, -108.03) * mm});
            skLineSegment(sketch, "E93.MirrorCS", {"start": v(-14.94, -120.03) * mm, "end": v(-14.88, -108) * mm});
            skSolve(sketch);
        }
        {
            var Q0;
            Q0=makeQuery(id+"F16.imprint","IMPRINT",FACE,{"disambiguationData":[TD([[makeQuery(id+"F16.imprint","IMPRINT",EDGE,{"derivedFrom":makeQuery(id+"F1.opExtrude","CAP_EDGE",EDGE,{"disambiguationData":[OSD([sQuery(id+"F0.wireOp",EDGE,"E1.left")])],"isStart":true})}),-1.0]])]});
            var Q1;
            Q1=makeQuery(id+"F16.imprint","IMPRINT",FACE,{"disambiguationData":[TD([[makeQuery(id+"F16.imprint","IMPRINT",EDGE,{"derivedFrom":sQuery(id+"F16.wireOp",EDGE,"E80")}),-1.0]])]});
            var Q2;
            Q2=makeQuery(id+"F16.imprint","IMPRINT",FACE,{"disambiguationData":[TD([[makeQuery(id+"F16.imprint","IMPRINT",EDGE,{"derivedFrom":sQuery(id+"F16.wireOp",EDGE,"E88.MirrorC")}),1.0]])]});
            var Q3;
            Q3=makeQuery(id+"F2.opExtrude","CAP_FACE",FACE,{"disambiguationData":[OSD([sQuery(id+"F0.wireOp",EDGE,"E12"),sQuery(id+"F0.wireOp",EDGE,"E13"),sQuery(id+"F0.wireOp",EDGE,"E14"),sQuery(id+"F0.wireOp",EDGE,"E15"),sQuery(id+"F0.wireOp",EDGE,"E17.filletArc"),sQuery(id+"F0.wireOp",EDGE,"E18.filletArc"),sQuery(id+"F0.wireOp",EDGE,"E19.filletArc"),sQuery(id+"F0.wireOp",EDGE,"E20.filletArc"),sQuery(id+"F0.wireOp",EDGE,"E25.0"),sQuery(id+"F0.wireOp",EDGE,"E25.1"),sQuery(id+"F0.wireOp",EDGE,"E25.2"),sQuery(id+"F0.wireOp",EDGE,"E25.3"),sQuery(id+"F0.wireOp",EDGE,"E25.4"),sQuery(id+"F0.wireOp",EDGE,"E25.5"),sQuery(id+"F0.wireOp",EDGE,"E25.6"),sQuery(id+"F0.wireOp",EDGE,"E25.7")])],"isStart":false});
            extrude(context, id + "F17", {"entities" : qUnion([Q0, Q1, Q2]), "endBound" : BoundingType.UP_TO_SURFACE, "endBoundEntityFace" : qUnion([Q3]), "depth" : 25 * mm});
        }
    });
